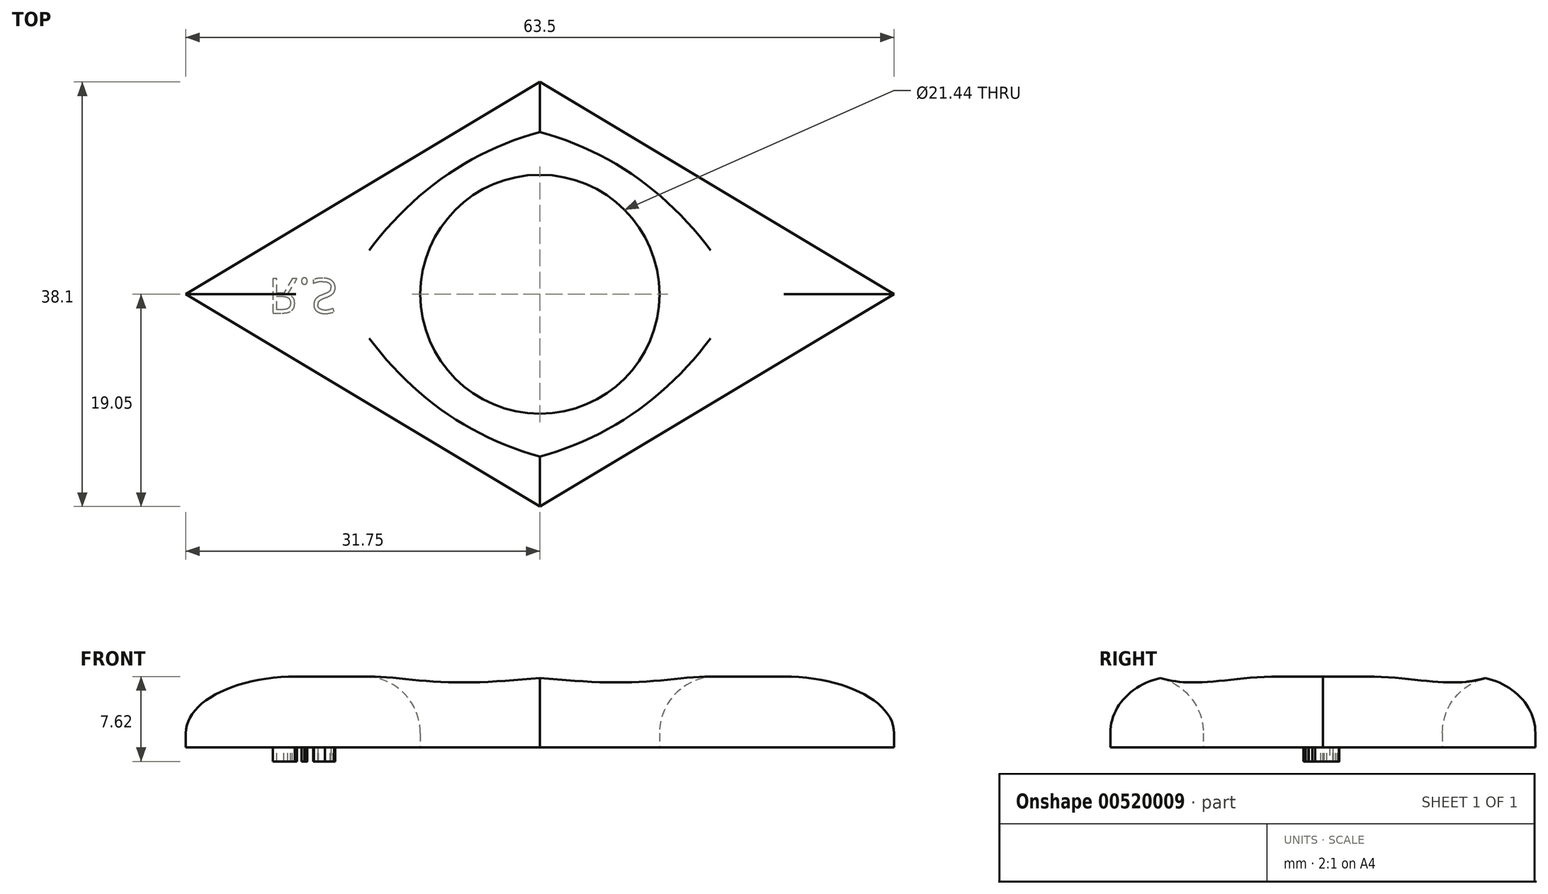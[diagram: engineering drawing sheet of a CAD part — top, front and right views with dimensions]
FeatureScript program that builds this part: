
annotation { "Feature Type Name" : "Feature", "Feature Type Description" : "" }
export const myFeature = defineFeature(function(context is Context, id is Id, definition is map)
    precondition{}
    {
        {
            var Q0;
            Q0=qCreatedBy(makeId("Top.planeOp"),FACE);
            var sketch = newSketch(context, id + "F0", { "sketchPlane" : qUnion([Q0])});
            skLineSegment(sketch, "E0.bottom", {"start": v(0, 0) * mm, "end": v(63.5, 0) * mm});
            skLineSegment(sketch, "E0.top", {"start": v(0, 38.1) * mm, "end": v(63.5, 38.1) * mm});
            skLineSegment(sketch, "E0.left", {"start": v(0, 0) * mm, "end": v(0, 38.1) * mm});
            skLineSegment(sketch, "E0.right", {"start": v(63.5, 0) * mm, "end": v(63.5, 38.1) * mm});
            skCircle(sketch, "E1", {"center": v(31.75, 19.05) * mm, "radius": 11.43 * mm});
            skPoint(sketch, "E1.centerSnap0", {"position": v(0, 19.05) * mm});
            skPoint(sketch, "E1.centerSnap1", {"position": v(31.75, 0) * mm});
            skSolve(sketch);
        }
        {
            var Q0;
            Q0=makeQuery(id+"F0.imprint","IMPRINT",FACE,{"disambiguationData":[TD([[makeQuery(id+"F0.imprint","IMPRINT",EDGE,{"derivedFrom":sQuery(id+"F0.wireOp",EDGE,"E0.bottom")}),1.0]])]});
            var sketch = newSketch(context, id + "F1", { "sketchPlane" : qUnion([Q0])});
            skLineSegment(sketch, "E2", {"start": v(31.75, 38.1) * mm, "end": v(0, 19.05) * mm});
            skPoint(sketch, "E2.endSnap0", {"position": v(31.75, 19.05) * mm});
            skPoint(sketch, "E3.end.orphan", {"position": v(0, 38.1) * mm});
            skPoint(sketch, "E4.end.orphan", {"position": v(31.75, 0) * mm});
            skLineSegment(sketch, "E5", {"start": v(31.75, 38.1) * mm, "end": v(31.75, 0) * mm});
            skLineSegment(sketch, "E6", {"start": v(0, 19.05) * mm, "end": v(63.5, 19.05) * mm});
            skLineSegment(sketch, "E7", {"start": v(31.75, 38.1) * mm, "end": v(63.5, 19.05) * mm});
            skLineSegment(sketch, "E8", {"start": v(31.75, 0) * mm, "end": v(63.5, 19.05) * mm});
            skLineSegment(sketch, "E9", {"start": v(31.75, 0) * mm, "end": v(0, 19.05) * mm});
            skSolve(sketch);
        }
        {
            var Q0;
            Q0 = qSketchRegion(id + "F1", true);
            extrude(context, id + "F2", {"entities" : qUnion([Q0]), "depth" : 25.4 * mm, "offsetDistance" : 25.4 * mm});
        }
        {
            var Q0;
            Q0=makeQuery(id+"F2.opExtrude","CAP_FACE",FACE,{"disambiguationData":[OSD([sQuery(id+"F1.wireOp",EDGE,"E2"),sQuery(id+"F1.wireOp",EDGE,"E7"),sQuery(id+"F1.wireOp",EDGE,"E8"),sQuery(id+"F1.wireOp",EDGE,"E9")])],"isStart":false});
            extrude(context, id + "F3", {"entities" : qUnion([Q0]), "operationType" : NewBodyOperationType.REMOVE, "oppositeDirection" : true, "depth" : 19.05 * mm, "offsetDistance" : 25.4 * mm});
        }
        {
            var Q0;
            Q0=sQuery(id+"F0.wireOp",VERTEX,"E1.center");
            var Q1;
            Q1=makeQuery(id+"F2.opExtrude","SWEPT_BODY",BODY,{"disambiguationData":[OSD([sQuery(id+"F1.wireOp",EDGE,"E2"),sQuery(id+"F1.wireOp",EDGE,"E7"),sQuery(id+"F1.wireOp",EDGE,"E8"),sQuery(id+"F1.wireOp",EDGE,"E9")])]});
            hole(context, id + "F4", {"style" : HoleStyle.SIMPLE, "endStyle" : HoleEndStyle.THROUGH, "oppositeDirection" : true, "holeDiameter" : 21.44 * mm, "isTappedThrough" : true, "tappedDepth" : 12.7 * mm, "tapClearance" : 3, "locations" : qUnion([Q0]), "scope" : qUnion([Q1])});
        }
        {
            var Q0;
            Q0=makeQuery(id+"F3.boolean.opBoolean","COPY",FACE,{"derivedFrom":makeQuery(id+"F3.opExtrude","CAP_FACE",FACE,{"disambiguationData":[OSD([sQuery(id+"F1.wireOp",EDGE,"E2"),sQuery(id+"F1.wireOp",EDGE,"E7"),sQuery(id+"F1.wireOp",EDGE,"E8"),sQuery(id+"F1.wireOp",EDGE,"E9")])],"isStart":false})});
            fillet(context, id + "F5", {"entities" : qUnion([Q0]), "radius" : 5.08 * mm, "tangentPropagation" : true, "allowEdgeOverflow" : false});
        }
        {
            var Q0;
            Q0=makeQuery(id+"F2.opExtrude","CAP_FACE",FACE,{"disambiguationData":[OSD([sQuery(id+"F1.wireOp",EDGE,"E2"),sQuery(id+"F1.wireOp",EDGE,"E7"),sQuery(id+"F1.wireOp",EDGE,"E8"),sQuery(id+"F1.wireOp",EDGE,"E9")])],"isStart":true});
            var sketch = newSketch(context, id + "F6", { "sketchPlane" : qUnion([Q0])});
            skText(sketch, "E10", { "text": "R.S", "fontName": "OpenSans-Regular.ttf"});
            const initialGuessF6  = {"E10": [0.00737, -0.02046, 1, 0, 0.00313]};
            skSetInitialGuess(sketch, initialGuessF6);
            skSolve(sketch);
        }
        {
            var Q0;
            Q0 = qSketchRegion(id + "F6", true);
            extrude(context, id + "F7", {"entities" : qUnion([Q0]), "operationType" : NewBodyOperationType.ADD, "depth" : 1.27 * mm, "offsetDistance" : 25.4 * mm});
        }
    });
